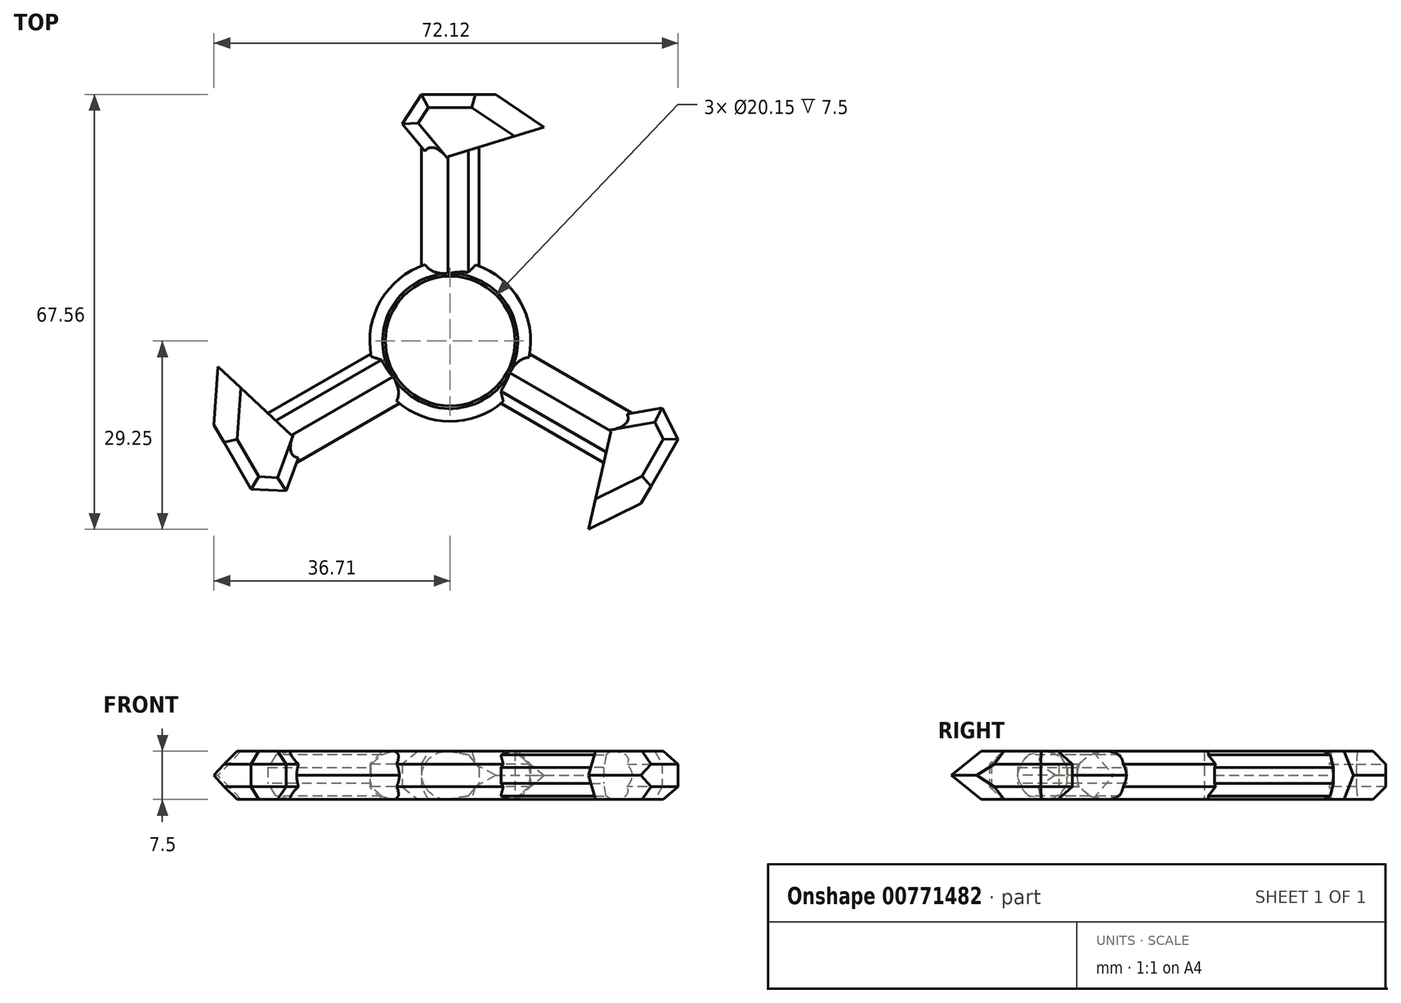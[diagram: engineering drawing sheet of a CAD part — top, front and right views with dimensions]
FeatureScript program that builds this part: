
annotation { "Feature Type Name" : "Feature", "Feature Type Description" : "" }
export const myFeature = defineFeature(function(context is Context, id is Id, definition is map)
    precondition{}
    {
        {
            var Q0;
            Q0=qCreatedBy(makeId("Top.planeOp"),FACE);
            var sketch = newSketch(context, id + "F0", { "sketchPlane" : qUnion([Q0])});
            skCircle(sketch, "E0", {"center": v(0, 0) * mm, "radius": 12.5 * mm});
            skLineSegment(sketch, "E1", {"start": v(0, 0) * mm, "end": v(-12.5, 0) * mm});
            skLineSegment(sketch, "E2", {"start": v(0, 0) * mm, "end": v(0, 12.5) * mm});
            skLineSegment(sketch, "E3", {"start": v(0, 0) * mm, "end": v(12.5, 0) * mm});
            skLineSegment(sketch, "E4", {"start": v(0, 0) * mm, "end": v(0, -12.5) * mm});
            skCircle(sketch, "E5.cCircle", {"center": v(0, 0) * mm, "radius": 7.71 * mm, "construction": true});
            skLineSegment(sketch, "E5.0", {"start": v(-4.45, 7.71) * mm, "end": v(4.45, 7.71) * mm});
            skLineSegment(sketch, "E5.1", {"start": v(4.45, 7.71) * mm, "end": v(8.9, 0) * mm});
            skLineSegment(sketch, "E5.2", {"start": v(8.9, 0) * mm, "end": v(4.45, -7.71) * mm});
            skLineSegment(sketch, "E5.3", {"start": v(4.45, -7.71) * mm, "end": v(-4.45, -7.71) * mm});
            skLineSegment(sketch, "E5.4", {"start": v(-4.45, -7.71) * mm, "end": v(-8.9, 0) * mm});
            skLineSegment(sketch, "E5.5", {"start": v(-8.9, 0) * mm, "end": v(-4.45, 7.71) * mm});
            skPoint(sketch, "E5.0.midPoint", {"position": v(0, 7.71) * mm});
            skLineSegment(sketch, "E6.top", {"start": v(-4.45, 33.71) * mm, "end": v(4.45, 33.71) * mm});
            skLineSegment(sketch, "E6.left", {"start": v(-4.45, 7.71) * mm, "end": v(-4.45, 33.71) * mm});
            skLineSegment(sketch, "E6.right", {"start": v(4.45, 7.71) * mm, "end": v(4.45, 33.71) * mm});
            skLineSegment(sketch, "E7", {"start": v(0, 0) * mm, "end": v(-6.68, 3.86) * mm});
            skLineSegment(sketch, "E8.MirrorCS", {"start": v(-8.9, 0) * mm, "end": v(-31.42, -13) * mm});
            skLineSegment(sketch, "E9.MirrorCS", {"start": v(-4.45, -7.71) * mm, "end": v(-26.97, -20.71) * mm});
            skLineSegment(sketch, "E10.MirrorCS", {"start": v(-31.42, -13) * mm, "end": v(-26.97, -20.71) * mm});
            skLineSegment(sketch, "E11.MirrorCS", {"start": v(8.9, 0) * mm, "end": v(31.42, -13) * mm});
            skLineSegment(sketch, "E12.MirrorCS", {"start": v(4.45, -7.71) * mm, "end": v(26.97, -20.71) * mm});
            skLineSegment(sketch, "E13.MirrorCS", {"start": v(31.42, -13) * mm, "end": v(26.97, -20.71) * mm});
            skLineSegment(sketch, "E14", {"start": v(-4.45, 33.71) * mm, "end": v(-7.45, 33.71) * mm});
            skLineSegment(sketch, "E15", {"start": v(-7.45, 33.71) * mm, "end": v(-4.45, 38.3) * mm});
            skLineSegment(sketch, "E16", {"start": v(-4.45, 38.3) * mm, "end": v(9.3, 38.3) * mm});
            skLineSegment(sketch, "E17", {"start": v(9.3, 38.3) * mm, "end": v(16.11, 33.71) * mm});
            skLineSegment(sketch, "E18", {"start": v(16.11, 33.71) * mm, "end": v(4.45, 30.13) * mm});
            skLineSegment(sketch, "E19", {"start": v(-7.45, 33.71) * mm, "end": v(-4.45, 30.13) * mm});
            skLineSegment(sketch, "E20.top", {"start": v(-26.98, -20.72) * mm, "end": v(-31.43, -13) * mm});
            skLineSegment(sketch, "E21", {"start": v(-26.98, -20.72) * mm, "end": v(-25.48, -23.31) * mm});
            skLineSegment(sketch, "E22", {"start": v(-25.48, -23.31) * mm, "end": v(-30.95, -23.01) * mm});
            skLineSegment(sketch, "E23", {"start": v(-30.95, -23.01) * mm, "end": v(-37.83, -11.1) * mm});
            skLineSegment(sketch, "E24", {"start": v(-37.83, -11.1) * mm, "end": v(-37.26, -2.9) * mm});
            skLineSegment(sketch, "E25", {"start": v(-37.26, -2.9) * mm, "end": v(-28.32, -11.2) * mm});
            skLineSegment(sketch, "E26", {"start": v(-25.48, -23.31) * mm, "end": v(-23.87, -18.92) * mm});
            skLineSegment(sketch, "E27.0", {"start": v(-23.87, -18.92) * mm, "end": v(-28.32, -11.2) * mm, "construction": true});
            skLineSegment(sketch, "E28.0", {"start": v(-26.98, -20.72) * mm, "end": v(-37.26, -2.9) * mm, "construction": true});
            skLineSegment(sketch, "E29.0", {"start": v(-26.98, -20.72) * mm, "end": v(-30.95, -23.01) * mm, "construction": true});
            skLineSegment(sketch, "E30.top", {"start": v(31.43, -13) * mm, "end": v(26.98, -20.72) * mm});
            skLineSegment(sketch, "E31", {"start": v(31.43, -13) * mm, "end": v(32.93, -10.4) * mm});
            skLineSegment(sketch, "E32", {"start": v(32.93, -10.4) * mm, "end": v(35.4, -15.3) * mm});
            skLineSegment(sketch, "E33", {"start": v(35.4, -15.3) * mm, "end": v(28.53, -27.2) * mm});
            skLineSegment(sketch, "E34", {"start": v(28.53, -27.2) * mm, "end": v(21.15, -30.81) * mm});
            skLineSegment(sketch, "E35", {"start": v(21.15, -30.81) * mm, "end": v(23.87, -18.92) * mm});
            skLineSegment(sketch, "E36", {"start": v(32.93, -10.4) * mm, "end": v(28.32, -11.2) * mm});
            skLineSegment(sketch, "E37.0", {"start": v(28.32, -11.2) * mm, "end": v(23.87, -18.92) * mm, "construction": true});
            skLineSegment(sketch, "E38.0", {"start": v(31.43, -13) * mm, "end": v(21.15, -30.81) * mm, "construction": true});
            skLineSegment(sketch, "E39.0", {"start": v(31.43, -13) * mm, "end": v(35.4, -15.3) * mm, "construction": true});
            skCircle(sketch, "E40", {"center": v(0, 0) * mm, "radius": 10.07 * mm});
            skSolve(sketch);
        }
        {
            var Q0;
            {var subQ4=sQuery(id+"F0.wireOp",EDGE,"E6.top");Q0=makeQuery(id+"F0.imprint","IMPRINT",FACE,{"disambiguationData":[TD([[makeQuery(id+"F0.imprint","IMPRINT",EDGE,{"derivedFrom":subQ4}),-1.0]])]});}
            var Q1;
            {var subQ0=sQuery(id+"F0.wireOp",EDGE,"E6.top");Q1=makeQuery(id+"F0.imprint","IMPRINT",FACE,{"disambiguationData":[TD([[makeQuery(id+"F0.imprint","IMPRINT",EDGE,{"derivedFrom":subQ0}),1.0]])]});}
            var Q2;
            {var subQ4=sQuery(id+"F0.wireOp",EDGE,"E1");var subQ5=sQuery(id+"F0.wireOp",EDGE,"E0");var subQ6=makeQuery(id+"F0.imprint","INTERSECT",VERTEX,{"derivedFrom":[subQ5,subQ4]});Q2=makeQuery(id+"F0.imprint","IMPRINT",FACE,{"disambiguationData":[TD([[makeQuery(id+"F0.imprint","IMPRINT",EDGE,{"disambiguationData":[TD([[subQ6,1.0]])],"derivedFrom":subQ5}),1.0]])]});}
            var Q3;
            {var subQ0=sQuery(id+"F0.wireOp",EDGE,"E2");var subQ1=sQuery(id+"F0.wireOp",EDGE,"E0");var subQ2=makeQuery(id+"F0.imprint","INTERSECT",VERTEX,{"derivedFrom":[subQ1,subQ0]});Q3=makeQuery(id+"F0.imprint","IMPRINT",FACE,{"disambiguationData":[TD([[makeQuery(id+"F0.imprint","IMPRINT",EDGE,{"disambiguationData":[TD([[subQ2,-1.0]])],"derivedFrom":subQ1}),1.0]])]});}
            var Q4;
            {var subQ0=sQuery(id+"F0.wireOp",EDGE,"E2");var subQ1=sQuery(id+"F0.wireOp",EDGE,"E0");var subQ2=makeQuery(id+"F0.imprint","INTERSECT",VERTEX,{"derivedFrom":[subQ1,subQ0]});Q4=makeQuery(id+"F0.imprint","IMPRINT",FACE,{"disambiguationData":[TD([[makeQuery(id+"F0.imprint","IMPRINT",EDGE,{"disambiguationData":[TD([[subQ2,1.0]])],"derivedFrom":subQ1}),1.0]])]});}
            var Q5;
            {var subQ0=sQuery(id+"F0.wireOp",EDGE,"E1");var subQ1=sQuery(id+"F0.wireOp",EDGE,"E0");var subQ2=makeQuery(id+"F0.imprint","INTERSECT",VERTEX,{"derivedFrom":[subQ1,subQ0]});Q5=makeQuery(id+"F0.imprint","IMPRINT",FACE,{"disambiguationData":[TD([[makeQuery(id+"F0.imprint","IMPRINT",EDGE,{"disambiguationData":[TD([[subQ2,-1.0]])],"derivedFrom":subQ1}),1.0]])]});}
            var Q6;
            {var subQ0=sQuery(id+"F0.wireOp",EDGE,"E4");var subQ1=sQuery(id+"F0.wireOp",EDGE,"E0");var subQ2=makeQuery(id+"F0.imprint","INTERSECT",VERTEX,{"derivedFrom":[subQ1,subQ0]});Q6=makeQuery(id+"F0.imprint","IMPRINT",FACE,{"disambiguationData":[TD([[makeQuery(id+"F0.imprint","IMPRINT",EDGE,{"disambiguationData":[TD([[subQ2,-1.0]])],"derivedFrom":subQ1}),1.0]])]});}
            var Q7;
            {var subQ0=sQuery(id+"F0.wireOp",EDGE,"E3");var subQ1=sQuery(id+"F0.wireOp",EDGE,"E0");var subQ2=makeQuery(id+"F0.imprint","INTERSECT",VERTEX,{"derivedFrom":[subQ1,subQ0]});Q7=makeQuery(id+"F0.imprint","IMPRINT",FACE,{"disambiguationData":[TD([[makeQuery(id+"F0.imprint","IMPRINT",EDGE,{"disambiguationData":[TD([[subQ2,1.0]])],"derivedFrom":subQ1}),1.0]])]});}
            var Q8;
            {var subQ0=sQuery(id+"F0.wireOp",EDGE,"E4");var subQ1=sQuery(id+"F0.wireOp",EDGE,"E0");var subQ2=makeQuery(id+"F0.imprint","INTERSECT",VERTEX,{"derivedFrom":[subQ1,subQ0]});Q8=makeQuery(id+"F0.imprint","IMPRINT",FACE,{"disambiguationData":[TD([[makeQuery(id+"F0.imprint","IMPRINT",EDGE,{"disambiguationData":[TD([[subQ2,1.0]])],"derivedFrom":subQ1}),1.0]])]});}
            var Q9;
            {var subQ4=sQuery(id+"F0.wireOp",EDGE,"E13.MirrorCS");Q9=makeQuery(id+"F0.imprint","IMPRINT",FACE,{"disambiguationData":[TD([[makeQuery(id+"F0.imprint","IMPRINT",EDGE,{"derivedFrom":subQ4}),-1.0]])]});}
            var Q10;
            {var subQ0=sQuery(id+"F0.wireOp",EDGE,"E13.MirrorCS");Q10=makeQuery(id+"F0.imprint","IMPRINT",FACE,{"disambiguationData":[TD([[makeQuery(id+"F0.imprint","IMPRINT",EDGE,{"derivedFrom":subQ0}),1.0]])]});}
            var Q11;
            {var subQ0=sQuery(id+"F0.wireOp",EDGE,"E14");Q11=makeQuery(id+"F0.imprint","IMPRINT",FACE,{"disambiguationData":[TD([[makeQuery(id+"F0.imprint","IMPRINT",EDGE,{"derivedFrom":subQ0}),1.0]])]});}
            var Q12;
            {var subQ4=sQuery(id+"F0.wireOp",EDGE,"E10.MirrorCS");Q12=makeQuery(id+"F0.imprint","IMPRINT",FACE,{"disambiguationData":[TD([[makeQuery(id+"F0.imprint","IMPRINT",EDGE,{"derivedFrom":subQ4}),1.0]])]});}
            var Q13;
            {var subQ0=sQuery(id+"F0.wireOp",EDGE,"E10.MirrorCS");Q13=makeQuery(id+"F0.imprint","IMPRINT",FACE,{"disambiguationData":[TD([[makeQuery(id+"F0.imprint","IMPRINT",EDGE,{"derivedFrom":subQ0}),-1.0]])]});}
            var Q14;
            {var subQ0=sQuery(id+"F0.wireOp",EDGE,"E3");var subQ1=sQuery(id+"F0.wireOp",EDGE,"E0");var subQ2=makeQuery(id+"F0.imprint","INTERSECT",VERTEX,{"derivedFrom":[subQ1,subQ0]});Q14=makeQuery(id+"F0.imprint","IMPRINT",FACE,{"disambiguationData":[TD([[makeQuery(id+"F0.imprint","IMPRINT",EDGE,{"disambiguationData":[TD([[subQ2,-1.0]])],"derivedFrom":subQ1}),1.0]])]});}
            var Q15;
            {var subQ0=sQuery(id+"F0.wireOp",EDGE,"E8.MirrorCS");var subQ1=sQuery(id+"F0.wireOp",EDGE,"E0");var subQ2=makeQuery(id+"F0.imprint","INTERSECT",VERTEX,{"derivedFrom":[subQ1,subQ0]});Q15=makeQuery(id+"F0.imprint","IMPRINT",FACE,{"disambiguationData":[TD([[makeQuery(id+"F0.imprint","IMPRINT",EDGE,{"disambiguationData":[TD([[subQ2,-1.0]])],"derivedFrom":subQ1}),1.0]])]});}
            var Q16;
            {var subQ0=sQuery(id+"F0.wireOp",EDGE,"E12.MirrorCS");var subQ1=sQuery(id+"F0.wireOp",EDGE,"E0");var subQ2=makeQuery(id+"F0.imprint","INTERSECT",VERTEX,{"derivedFrom":[subQ1,subQ0]});Q16=makeQuery(id+"F0.imprint","IMPRINT",FACE,{"disambiguationData":[TD([[makeQuery(id+"F0.imprint","IMPRINT",EDGE,{"disambiguationData":[TD([[subQ2,-1.0]])],"derivedFrom":subQ1}),1.0]])]});}
            extrude(context, id + "F1", {"entities" : qUnion([Q0, Q1, Q2, Q3, Q4, Q5, Q6, Q7, Q8, Q9, Q10, Q11, Q12, Q13, Q14, Q15, Q16]), "endBound" : BoundingType.SYMMETRIC, "depth" : 7.5 * mm, "offsetDistance" : 25 * mm});
        }
        {
            var Q0;
            Q0=makeQuery(id+"F1.opExtrude","CAP_EDGE",EDGE,{"disambiguationData":[OSD([sQuery(id+"F0.wireOp",EDGE,"E6.left")])],"isStart":false});
            var Q1;
            Q1=makeQuery(id+"F1.opExtrude","CAP_EDGE",EDGE,{"disambiguationData":[OSD([sQuery(id+"F0.wireOp",EDGE,"E6.left")])],"isStart":true});
            var Q2;
            Q2=makeQuery(id+"F1.opExtrude","CAP_EDGE",EDGE,{"disambiguationData":[OSD([sQuery(id+"F0.wireOp",EDGE,"E9.MirrorCS")])],"isStart":false});
            var Q3;
            Q3=makeQuery(id+"F1.opExtrude","CAP_EDGE",EDGE,{"disambiguationData":[OSD([sQuery(id+"F0.wireOp",EDGE,"E11.MirrorCS")])],"isStart":false});
            var Q4;
            Q4=makeQuery(id+"F1.opExtrude","CAP_EDGE",EDGE,{"disambiguationData":[OSD([sQuery(id+"F0.wireOp",EDGE,"E11.MirrorCS")])],"isStart":true});
            var Q5;
            Q5=makeQuery(id+"F1.opExtrude","CAP_EDGE",EDGE,{"disambiguationData":[OSD([sQuery(id+"F0.wireOp",EDGE,"E9.MirrorCS")])],"isStart":true});
            fillet(context, id + "F2", {"entities" : qUnion([Q0, Q1, Q2, Q3, Q4, Q5]), "radius" : 4 * mm, "tangentPropagation" : true, "allowEdgeOverflow" : false});
        }
        {
            var Q0;
            Q0=makeQuery(id+"F1.opExtrude","CAP_EDGE",EDGE,{"disambiguationData":[OSD([sQuery(id+"F0.wireOp",EDGE,"E6.right")])],"isStart":false});
            var Q1;
            Q1=makeQuery(id+"F1.opExtrude","CAP_EDGE",EDGE,{"disambiguationData":[OSD([sQuery(id+"F0.wireOp",EDGE,"E6.right")])],"isStart":true});
            var Q2;
            Q2=makeQuery(id+"F1.opExtrude","CAP_EDGE",EDGE,{"disambiguationData":[OSD([sQuery(id+"F0.wireOp",EDGE,"E12.MirrorCS")])],"isStart":false});
            var Q3;
            Q3=makeQuery(id+"F1.opExtrude","CAP_EDGE",EDGE,{"disambiguationData":[OSD([sQuery(id+"F0.wireOp",EDGE,"E8.MirrorCS")])],"isStart":false});
            chamfer(context, id + "F3", {"entities" : qUnion([Q0, Q1, Q2, Q3]), "chamferType" : ChamferType.OFFSET_ANGLE, "width" : 4.8 * mm, "oppositeDirection" : false, "angle" : 10 * degree, "tangentPropagation" : true});
        }
        {
            var Q0;
            Q0=makeQuery(id+"F1.opExtrude","CAP_EDGE",EDGE,{"disambiguationData":[OSD([sQuery(id+"F0.wireOp",EDGE,"E12.MirrorCS")])],"isStart":true});
            var Q1;
            Q1=makeQuery(id+"F1.opExtrude","CAP_EDGE",EDGE,{"disambiguationData":[OSD([sQuery(id+"F0.wireOp",EDGE,"E8.MirrorCS")])],"isStart":true});
            chamfer(context, id + "F4", {"entities" : qUnion([Q0, Q1]), "chamferType" : ChamferType.OFFSET_ANGLE, "width" : 4.8 * mm, "oppositeDirection" : true, "angle" : 10 * degree, "tangentPropagation" : true});
        }
        {
            var Q0;
            {var subQ0=sQuery(id+"F0.wireOp",EDGE,"E0");var subQ1=makeQuery(id+"F0.imprint","INTERSECT",VERTEX,{"derivedFrom":[subQ0,sQuery(id+"F0.wireOp",EDGE,"E1")]});Q0=makeQuery(id+"F1.opExtrude","CAP_EDGE",EDGE,{"disambiguationData":[OSD([subQ0]),TDD([makeQuery(id+"F0.imprint","IMPRINT",EDGE,{"disambiguationData":[TD([[subQ1,1.0]])],"derivedFrom":subQ0}),makeQuery(id+"F0.imprint","IMPRINT",EDGE,{"disambiguationData":[TD([[subQ1,-1.0]])],"derivedFrom":subQ0})])],"isStart":true});}
            var Q1;
            {var subQ0=sQuery(id+"F0.wireOp",EDGE,"E0");var subQ1=makeQuery(id+"F0.imprint","INTERSECT",VERTEX,{"derivedFrom":[subQ0,sQuery(id+"F0.wireOp",EDGE,"E1")]});Q1=makeQuery(id+"F1.opExtrude","CAP_EDGE",EDGE,{"disambiguationData":[OSD([subQ0]),TDD([makeQuery(id+"F0.imprint","IMPRINT",EDGE,{"disambiguationData":[TD([[subQ1,1.0]])],"derivedFrom":subQ0}),makeQuery(id+"F0.imprint","IMPRINT",EDGE,{"disambiguationData":[TD([[subQ1,-1.0]])],"derivedFrom":subQ0})])],"isStart":false});}
            var Q2;
            {var subQ0=sQuery(id+"F0.wireOp",EDGE,"E0");var subQ1=makeQuery(id+"F0.imprint","INTERSECT",VERTEX,{"derivedFrom":[subQ0,sQuery(id+"F0.wireOp",EDGE,"E4")]});Q2=makeQuery(id+"F1.opExtrude","CAP_EDGE",EDGE,{"disambiguationData":[OSD([subQ0]),TDD([makeQuery(id+"F0.imprint","IMPRINT",EDGE,{"disambiguationData":[TD([[subQ1,1.0]])],"derivedFrom":subQ0}),makeQuery(id+"F0.imprint","IMPRINT",EDGE,{"disambiguationData":[TD([[subQ1,-1.0]])],"derivedFrom":subQ0})])],"isStart":false});}
            var Q3;
            {var subQ0=sQuery(id+"F0.wireOp",EDGE,"E0");var subQ1=makeQuery(id+"F0.imprint","INTERSECT",VERTEX,{"derivedFrom":[subQ0,sQuery(id+"F0.wireOp",EDGE,"E4")]});Q3=makeQuery(id+"F1.opExtrude","CAP_EDGE",EDGE,{"disambiguationData":[OSD([subQ0]),TDD([makeQuery(id+"F0.imprint","IMPRINT",EDGE,{"disambiguationData":[TD([[subQ1,1.0]])],"derivedFrom":subQ0}),makeQuery(id+"F0.imprint","IMPRINT",EDGE,{"disambiguationData":[TD([[subQ1,-1.0]])],"derivedFrom":subQ0})])],"isStart":true});}
            var Q4;
            {var subQ0=sQuery(id+"F0.wireOp",EDGE,"E0");var subQ1=makeQuery(id+"F0.imprint","INTERSECT",VERTEX,{"derivedFrom":[subQ0,sQuery(id+"F0.wireOp",EDGE,"E3")]});Q4=makeQuery(id+"F1.opExtrude","CAP_EDGE",EDGE,{"disambiguationData":[OSD([subQ0]),TDD([makeQuery(id+"F0.imprint","IMPRINT",EDGE,{"disambiguationData":[TD([[subQ1,-1.0]])],"derivedFrom":subQ0}),makeQuery(id+"F0.imprint","IMPRINT",EDGE,{"disambiguationData":[TD([[subQ1,1.0]])],"derivedFrom":subQ0})])],"isStart":false});}
            var Q5;
            {var subQ0=sQuery(id+"F0.wireOp",EDGE,"E0");var subQ1=makeQuery(id+"F0.imprint","INTERSECT",VERTEX,{"derivedFrom":[subQ0,sQuery(id+"F0.wireOp",EDGE,"E3")]});Q5=makeQuery(id+"F1.opExtrude","CAP_EDGE",EDGE,{"disambiguationData":[OSD([subQ0]),TDD([makeQuery(id+"F0.imprint","IMPRINT",EDGE,{"disambiguationData":[TD([[subQ1,-1.0]])],"derivedFrom":subQ0}),makeQuery(id+"F0.imprint","IMPRINT",EDGE,{"disambiguationData":[TD([[subQ1,1.0]])],"derivedFrom":subQ0})])],"isStart":true});}
            chamfer(context, id + "F5", {"entities" : qUnion([Q0, Q1, Q2, Q3, Q4, Q5]), "width" : 2 * mm, "tangentPropagation" : true});
        }
        {
            var Q0;
            Q0=makeQuery(id+"F1.opExtrude","CAP_EDGE",EDGE,{"disambiguationData":[OSD([sQuery(id+"F0.wireOp",EDGE,"E15")])],"isStart":true});
            var Q1;
            Q1=makeQuery(id+"F1.opExtrude","CAP_EDGE",EDGE,{"disambiguationData":[OSD([sQuery(id+"F0.wireOp",EDGE,"E15")])],"isStart":false});
            var Q2;
            Q2=makeQuery(id+"F1.opExtrude","CAP_EDGE",EDGE,{"disambiguationData":[OSD([sQuery(id+"F0.wireOp",EDGE,"E19")])],"isStart":true});
            var Q3;
            Q3=makeQuery(id+"F1.opExtrude","CAP_EDGE",EDGE,{"disambiguationData":[OSD([sQuery(id+"F0.wireOp",EDGE,"E19")])],"isStart":false});
            var Q4;
            Q4=makeQuery(id+"F1.opExtrude","CAP_EDGE",EDGE,{"disambiguationData":[OSD([sQuery(id+"F0.wireOp",EDGE,"E26")])],"isStart":true});
            var Q5;
            Q5=makeQuery(id+"F1.opExtrude","CAP_EDGE",EDGE,{"disambiguationData":[OSD([sQuery(id+"F0.wireOp",EDGE,"E26")])],"isStart":false});
            var Q6;
            Q6=makeQuery(id+"F1.opExtrude","CAP_EDGE",EDGE,{"disambiguationData":[OSD([sQuery(id+"F0.wireOp",EDGE,"E22")])],"isStart":false});
            var Q7;
            Q7=makeQuery(id+"F1.opExtrude","CAP_EDGE",EDGE,{"disambiguationData":[OSD([sQuery(id+"F0.wireOp",EDGE,"E22")])],"isStart":true});
            var Q8;
            Q8=makeQuery(id+"F1.opExtrude","CAP_EDGE",EDGE,{"disambiguationData":[OSD([sQuery(id+"F0.wireOp",EDGE,"E23")])],"isStart":true});
            var Q9;
            Q9=makeQuery(id+"F1.opExtrude","CAP_EDGE",EDGE,{"disambiguationData":[OSD([sQuery(id+"F0.wireOp",EDGE,"E23")])],"isStart":false});
            var Q10;
            Q10=makeQuery(id+"F1.opExtrude","CAP_EDGE",EDGE,{"disambiguationData":[OSD([sQuery(id+"F0.wireOp",EDGE,"E16")])],"isStart":true});
            var Q11;
            Q11=makeQuery(id+"F1.opExtrude","CAP_EDGE",EDGE,{"disambiguationData":[OSD([sQuery(id+"F0.wireOp",EDGE,"E16")])],"isStart":false});
            var Q12;
            {var subQ0=sQuery(id+"F0.wireOp",EDGE,"E8.MirrorCS");Q12=makeQuery(id+"F3.opChamfer","BLEND_EDGE",EDGE,{"blendedFrom":[makeQuery(id+"F1.opExtrude","CAP_EDGE",EDGE,{"disambiguationData":[OSD([subQ0])],"isStart":false}),makeQuery(id+"F1.opExtrude","SWEPT_FACE",FACE,{"disambiguationData":[OSD([subQ0])]})],"blendedInto":[makeQuery(id+"F1.opExtrude","SWEPT_FACE",FACE,{"disambiguationData":[OSD([subQ0])]})]});}
            var Q13;
            {var subQ0=sQuery(id+"F0.wireOp",EDGE,"E8.MirrorCS");Q13=makeQuery(id+"F4.opChamfer","BLEND_EDGE",EDGE,{"blendedFrom":[makeQuery(id+"F1.opExtrude","CAP_EDGE",EDGE,{"disambiguationData":[OSD([subQ0])],"isStart":true}),makeQuery(id+"F1.opExtrude","SWEPT_FACE",FACE,{"disambiguationData":[OSD([subQ0])]})],"blendedInto":[makeQuery(id+"F1.opExtrude","SWEPT_FACE",FACE,{"disambiguationData":[OSD([subQ0])]})]});}
            var Q14;
            {var subQ0=sQuery(id+"F0.wireOp",EDGE,"E6.right");Q14=makeQuery(id+"F3.opChamfer","BLEND_EDGE",EDGE,{"blendedFrom":[makeQuery(id+"F1.opExtrude","CAP_EDGE",EDGE,{"disambiguationData":[OSD([subQ0])],"isStart":false}),makeQuery(id+"F1.opExtrude","SWEPT_FACE",FACE,{"disambiguationData":[OSD([subQ0])]})],"blendedInto":[makeQuery(id+"F1.opExtrude","SWEPT_FACE",FACE,{"disambiguationData":[OSD([subQ0])]})]});}
            var Q15;
            {var subQ0=sQuery(id+"F0.wireOp",EDGE,"E6.right");Q15=makeQuery(id+"F3.opChamfer","BLEND_EDGE",EDGE,{"blendedFrom":[makeQuery(id+"F1.opExtrude","CAP_EDGE",EDGE,{"disambiguationData":[OSD([subQ0])],"isStart":true}),makeQuery(id+"F1.opExtrude","SWEPT_FACE",FACE,{"disambiguationData":[OSD([subQ0])]})],"blendedInto":[makeQuery(id+"F1.opExtrude","SWEPT_FACE",FACE,{"disambiguationData":[OSD([subQ0])]})]});}
            var Q16;
            Q16=makeQuery(id+"F1.opExtrude","CAP_EDGE",EDGE,{"disambiguationData":[OSD([sQuery(id+"F0.wireOp",EDGE,"E36")])],"isStart":false});
            var Q17;
            Q17=makeQuery(id+"F1.opExtrude","CAP_EDGE",EDGE,{"disambiguationData":[OSD([sQuery(id+"F0.wireOp",EDGE,"E32")])],"isStart":false});
            var Q18;
            Q18=makeQuery(id+"F1.opExtrude","CAP_EDGE",EDGE,{"disambiguationData":[OSD([sQuery(id+"F0.wireOp",EDGE,"E33")])],"isStart":false});
            var Q19;
            Q19=makeQuery(id+"F1.opExtrude","CAP_EDGE",EDGE,{"disambiguationData":[OSD([sQuery(id+"F0.wireOp",EDGE,"E36")])],"isStart":true});
            var Q20;
            Q20=makeQuery(id+"F1.opExtrude","CAP_EDGE",EDGE,{"disambiguationData":[OSD([sQuery(id+"F0.wireOp",EDGE,"E32")])],"isStart":true});
            var Q21;
            Q21=makeQuery(id+"F1.opExtrude","CAP_EDGE",EDGE,{"disambiguationData":[OSD([sQuery(id+"F0.wireOp",EDGE,"E33")])],"isStart":true});
            var Q22;
            {var subQ0=sQuery(id+"F0.wireOp",EDGE,"E12.MirrorCS");Q22=makeQuery(id+"F4.opChamfer","BLEND_EDGE",EDGE,{"blendedFrom":[makeQuery(id+"F1.opExtrude","CAP_EDGE",EDGE,{"disambiguationData":[OSD([subQ0])],"isStart":true}),makeQuery(id+"F1.opExtrude","SWEPT_FACE",FACE,{"disambiguationData":[OSD([subQ0])]})],"blendedInto":[makeQuery(id+"F1.opExtrude","SWEPT_FACE",FACE,{"disambiguationData":[OSD([subQ0])]})]});}
            var Q23;
            {var subQ0=sQuery(id+"F0.wireOp",EDGE,"E12.MirrorCS");Q23=makeQuery(id+"F3.opChamfer","BLEND_EDGE",EDGE,{"blendedFrom":[makeQuery(id+"F1.opExtrude","CAP_EDGE",EDGE,{"disambiguationData":[OSD([subQ0])],"isStart":false}),makeQuery(id+"F1.opExtrude","SWEPT_FACE",FACE,{"disambiguationData":[OSD([subQ0])]})],"blendedInto":[makeQuery(id+"F1.opExtrude","SWEPT_FACE",FACE,{"disambiguationData":[OSD([subQ0])]})]});}
            chamfer(context, id + "F6", {"entities" : qUnion([Q0, Q1, Q2, Q3, Q4, Q5, Q6, Q7, Q8, Q9, Q10, Q11, Q12, Q13, Q14, Q15, Q16, Q17, Q18, Q19, Q20, Q21, Q22, Q23]), "width" : 2 * mm, "tangentPropagation" : true});
        }
        {
            var Q0;
            Q0=makeQuery(id+"F1.opExtrude","CAP_EDGE",EDGE,{"disambiguationData":[OSD([sQuery(id+"F0.wireOp",EDGE,"E34")])],"isStart":false});
            var Q1;
            Q1=makeQuery(id+"F1.opExtrude","CAP_EDGE",EDGE,{"disambiguationData":[OSD([sQuery(id+"F0.wireOp",EDGE,"E34")])],"isStart":true});
            var Q2;
            Q2=makeQuery(id+"F1.opExtrude","CAP_EDGE",EDGE,{"disambiguationData":[OSD([sQuery(id+"F0.wireOp",EDGE,"E24")])],"isStart":false});
            var Q3;
            Q3=makeQuery(id+"F1.opExtrude","CAP_EDGE",EDGE,{"disambiguationData":[OSD([sQuery(id+"F0.wireOp",EDGE,"E24")])],"isStart":true});
            var Q4;
            Q4=makeQuery(id+"F1.opExtrude","CAP_EDGE",EDGE,{"disambiguationData":[OSD([sQuery(id+"F0.wireOp",EDGE,"E17")])],"isStart":false});
            var Q5;
            Q5=makeQuery(id+"F1.opExtrude","CAP_EDGE",EDGE,{"disambiguationData":[OSD([sQuery(id+"F0.wireOp",EDGE,"E17")])],"isStart":true});
            chamfer(context, id + "F7", {"entities" : qUnion([Q0, Q1, Q2, Q3, Q4, Q5]), "width" : 5 * mm, "tangentPropagation" : true});
        }
    });
